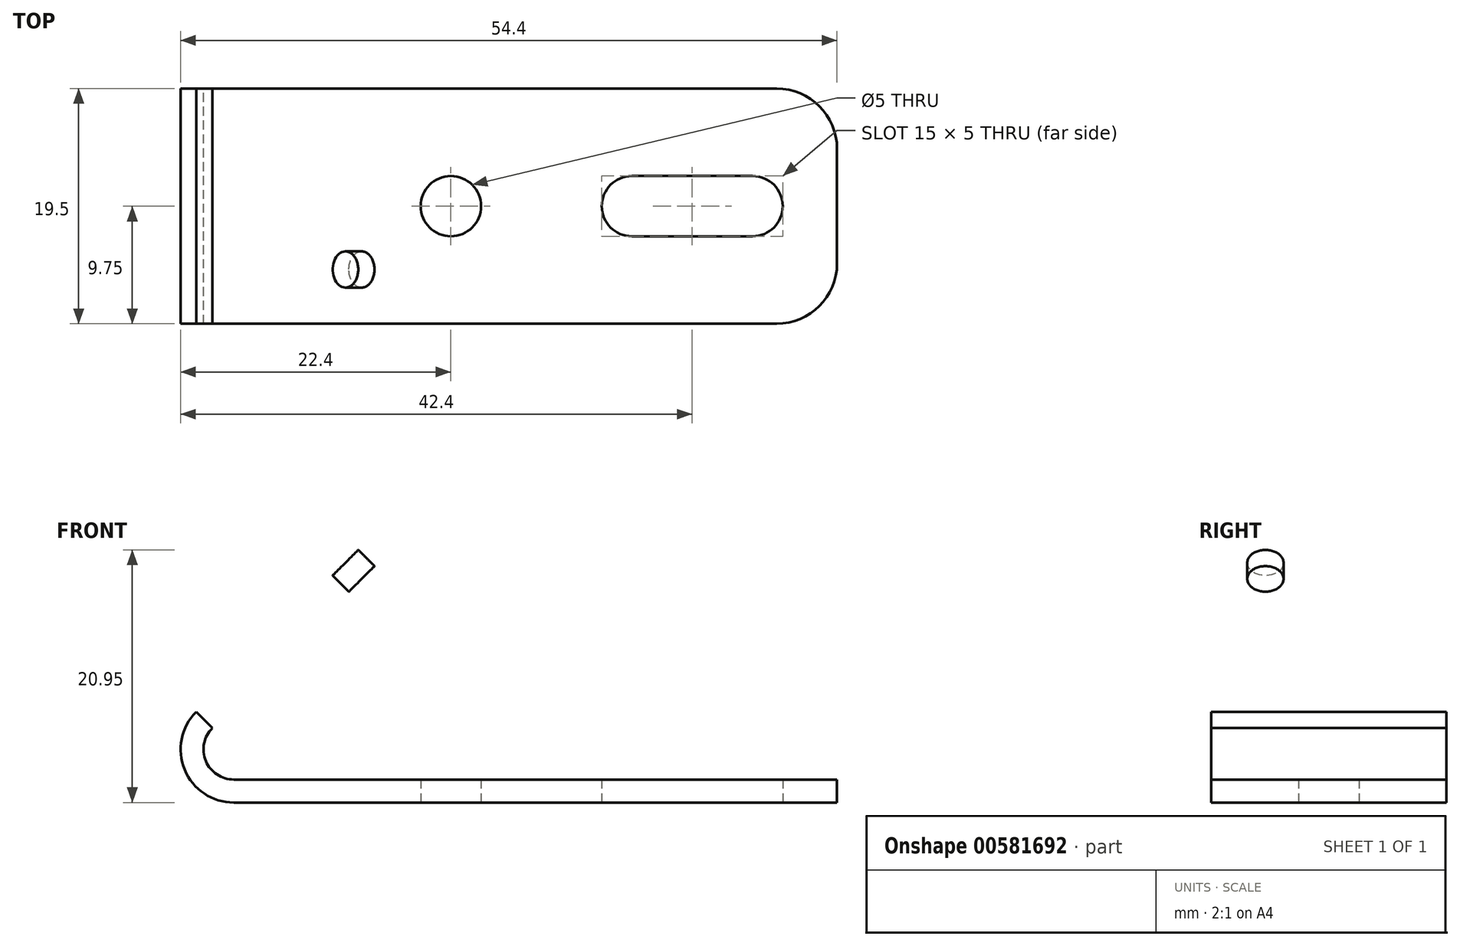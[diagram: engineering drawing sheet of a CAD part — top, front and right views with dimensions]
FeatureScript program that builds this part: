
annotation { "Feature Type Name" : "Feature", "Feature Type Description" : "" }
export const myFeature = defineFeature(function(context is Context, id is Id, definition is map)
    precondition{}
    {
        {
            var Q0;
            Q0=qCreatedBy(makeId("Front.planeOp"),FACE);
            var sketch = newSketch(context, id + "F0", { "sketchPlane" : qUnion([Q0])});
            skArc(sketch, "E0", {"start": v(-3.11, 3.11) * mm, "mid": v(-4.07, -1.68) * mm, "end": v(0, -4.4) * mm});
            skLineSegment(sketch, "E1", {"start": v(0, 0) * mm, "end": v(50, 0) * mm, "construction": true});
            skLineSegment(sketch, "E2", {"start": v(0, 0) * mm, "end": v(17.68, 17.68) * mm, "construction": true});
            skLineSegment(sketch, "E3", {"start": v(-3.11, 3.11) * mm, "end": v(14.57, 20.79) * mm});
            skLineSegment(sketch, "E4", {"start": v(0, -4.4) * mm, "end": v(50, -4.4) * mm});
            skLineSegment(sketch, "E5", {"start": v(14.57, 20.79) * mm, "end": v(15.9, 19.45) * mm});
            skLineSegment(sketch, "E6", {"start": v(50, -4.4) * mm, "end": v(50, -2.5) * mm});
            skArc(sketch, "E7", {"start": v(-1.77, 1.77) * mm, "mid": v(-2.3, -0.96) * mm, "end": v(0, -2.5) * mm});
            skLineSegment(sketch, "E8", {"start": v(50, -2.5) * mm, "end": v(0, -2.5) * mm});
            skLineSegment(sketch, "E9", {"start": v(15.9, 19.45) * mm, "end": v(-1.77, 1.77) * mm});
            skSolve(sketch);
        }
        {
            var Q0;
            Q0=makeQuery(id+"F0.imprint","IMPRINT",FACE,{"disambiguationData":[TD([[makeQuery(id+"F0.imprint","IMPRINT",EDGE,{"derivedFrom":sQuery(id+"F0.wireOp",EDGE,"E0")}),1.0]])]});
            extrude(context, id + "F1", {"entities" : qUnion([Q0]), "endBound" : BoundingType.SYMMETRIC, "depth" : 19.5 * mm, "offsetDistance" : 25 * mm});
        }
        {
            var Q0;
            Q0=makeQuery(id+"F1.opExtrude","SWEPT_FACE",FACE,{"disambiguationData":[OSD([sQuery(id+"F0.wireOp",EDGE,"E4")])]});
            var sketch = newSketch(context, id + "F2", { "sketchPlane" : qUnion([Q0])});
            skLineSegment(sketch, "E10", {"start": v(50, 0) * mm, "end": v(18, 0) * mm, "construction": true});
            skCircle(sketch, "E11", {"center": v(18, 0) * mm, "radius": 2.5 * mm});
            skArc(sketch, "E12", {"start": v(33, 2.5) * mm, "mid": v(30.5, 0) * mm, "end": v(33, -2.5) * mm});
            skArc(sketch, "E13", {"start": v(43, -2.5) * mm, "mid": v(45.5, 0) * mm, "end": v(43, 2.5) * mm});
            skLineSegment(sketch, "E14", {"start": v(33, 2.5) * mm, "end": v(43, 2.5) * mm});
            skLineSegment(sketch, "E15", {"start": v(33, -2.5) * mm, "end": v(43, -2.5) * mm});
            skSolve(sketch);
        }
        {
            var Q0;
            Q0=makeQuery(id+"F2.imprint","IMPRINT",FACE,{"disambiguationData":[TD([[makeQuery(id+"F2.imprint","IMPRINT",EDGE,{"derivedFrom":sQuery(id+"F2.wireOp",EDGE,"E11")}),1.0]])]});
            var Q1;
            Q1=makeQuery(id+"F2.imprint","IMPRINT",FACE,{"disambiguationData":[TD([[makeQuery(id+"F2.imprint","IMPRINT",EDGE,{"derivedFrom":sQuery(id+"F2.wireOp",EDGE,"E12")}),1.0]])]});
            extrude(context, id + "F3", {"entities" : qUnion([Q0, Q1]), "operationType" : NewBodyOperationType.REMOVE, "oppositeDirection" : true, "depth" : 2 * mm, "offsetDistance" : 25 * mm});
        }
        {
            var Q0;
            Q0=makeQuery(id+"F1.opExtrude","SWEPT_FACE",FACE,{"disambiguationData":[OSD([sQuery(id+"F0.wireOp",EDGE,"E3")])]});
            var sketch = newSketch(context, id + "F4", { "sketchPlane" : qUnion([Q0])});
            skCircle(sketch, "E16", {"center": v(-5.25, 17.5) * mm, "radius": 1.5 * mm});
            skPoint(sketch, "E17.endSnap0", {"position": v(0, 25) * mm});
            skLineSegment(sketch, "E18", {"start": v(0, 25) * mm, "end": v(0, 0) * mm, "construction": true});
            skCircle(sketch, "E19.MirrorC", {"center": v(5.25, 17.5) * mm, "radius": 1.5 * mm});
            skSolve(sketch);
        }
        {
            var Q0;
            Q0=makeQuery(id+"F4.imprint","IMPRINT",FACE,{"disambiguationData":[TD([[makeQuery(id+"F4.imprint","IMPRINT",EDGE,{"derivedFrom":sQuery(id+"F4.wireOp",EDGE,"E16")}),1.0]])]});
            var Q1;
            Q1=makeQuery(id+"F4.imprint","IMPRINT",FACE,{"disambiguationData":[TD([[makeQuery(id+"F4.imprint","IMPRINT",EDGE,{"derivedFrom":sQuery(id+"F4.wireOp",EDGE,"E19.MirrorC")}),-1.0]])]});
            extrude(context, id + "F5", {"entities" : qUnion([Q0, Q1]), "operationType" : NewBodyOperationType.REMOVE, "oppositeDirection" : true, "depth" : 2 * mm, "offsetDistance" : 25 * mm});
        }
        {
            var Q0;
            Q0=makeQuery(id+"F1.opExtrude","CAP_EDGE",EDGE,{"disambiguationData":[OSD([sQuery(id+"F0.wireOp",EDGE,"E5")])],"isStart":false});
            var Q1;
            Q1=makeQuery(id+"F1.opExtrude","CAP_EDGE",EDGE,{"disambiguationData":[OSD([sQuery(id+"F0.wireOp",EDGE,"E5")])],"isStart":true});
            var Q2;
            Q2=makeQuery(id+"F1.opExtrude","CAP_EDGE",EDGE,{"disambiguationData":[OSD([sQuery(id+"F0.wireOp",EDGE,"E6")])],"isStart":true});
            var Q3;
            Q3=makeQuery(id+"F1.opExtrude","CAP_EDGE",EDGE,{"disambiguationData":[OSD([sQuery(id+"F0.wireOp",EDGE,"E6")])],"isStart":false});
            fillet(context, id + "F6", {"entities" : qUnion([Q0, Q1, Q2, Q3]), "radius" : 5 * mm, "tangentPropagation" : true, "allowEdgeOverflow" : false});
        }
    });
